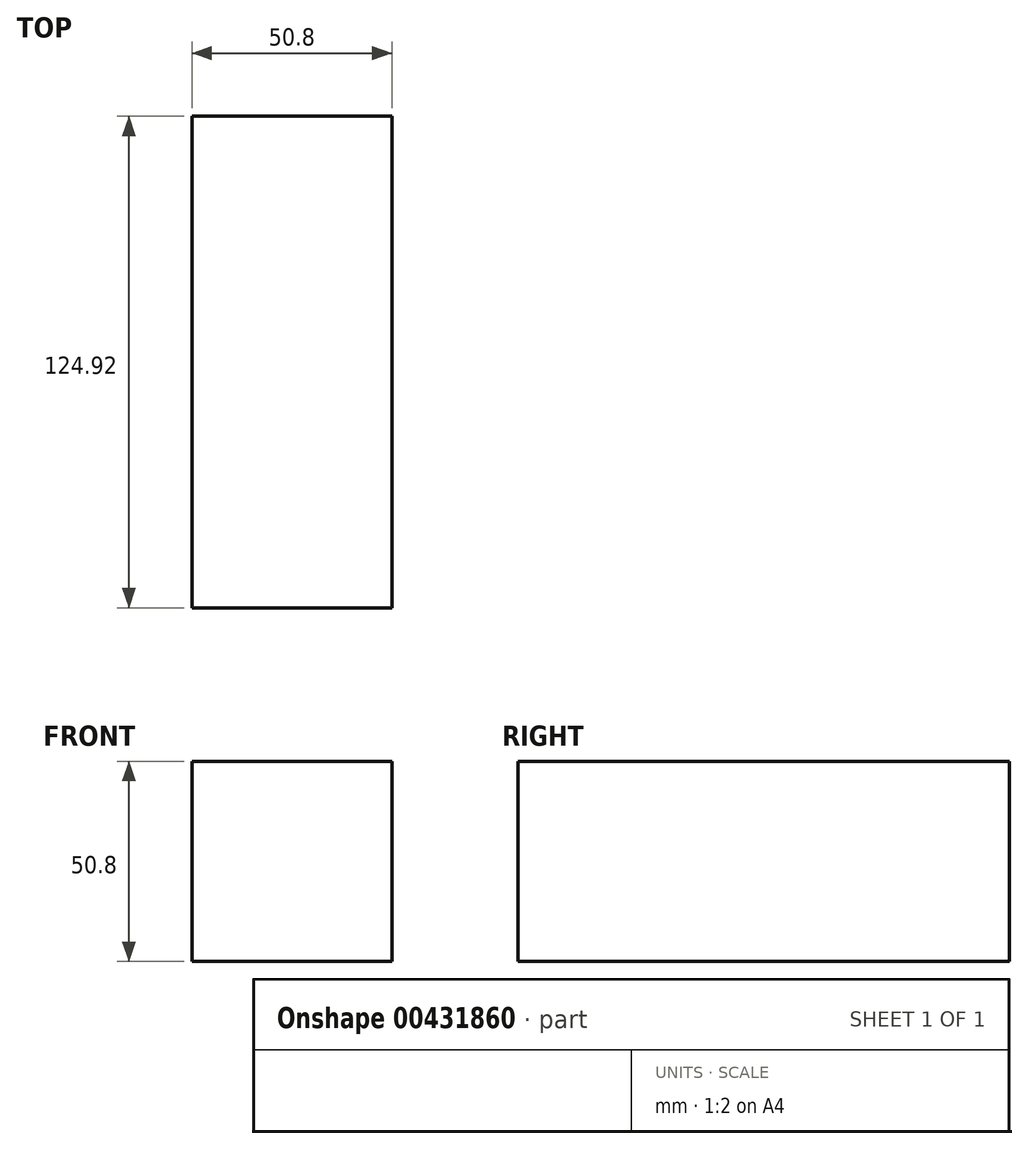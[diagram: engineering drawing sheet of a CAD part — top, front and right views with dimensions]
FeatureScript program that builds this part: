
annotation { "Feature Type Name" : "Feature", "Feature Type Description" : "" }
export const myFeature = defineFeature(function(context is Context, id is Id, definition is map)
    precondition{}
    {
        {
            var Q0;
            Q0=qCreatedBy(makeId("Front.planeOp"),FACE);
            var sketch = newSketch(context, id + "F0", { "sketchPlane" : qUnion([Q0])});
            skLineSegment(sketch, "E0.bottom", {"start": v(0, 0) * mm, "end": v(50.8, 0) * mm});
            skLineSegment(sketch, "E0.top", {"start": v(0, 50.8) * mm, "end": v(50.8, 50.8) * mm});
            skLineSegment(sketch, "E0.left", {"start": v(0, 0) * mm, "end": v(0, 50.8) * mm});
            skLineSegment(sketch, "E0.right", {"start": v(50.8, 0) * mm, "end": v(50.8, 50.8) * mm});
            skSolve(sketch);
        }
        {
            var Q0;
            Q0=makeQuery(id+"F0.imprint","IMPRINT",FACE,{"disambiguationData":[TD([[makeQuery(id+"F0.imprint","IMPRINT",EDGE,{"derivedFrom":sQuery(id+"F0.wireOp",EDGE,"E0.bottom")}),1.0]])]});
            extrude(context, id + "F1", {"entities" : qUnion([Q0]), "depth" : 124.92 * mm});
        }
    });
